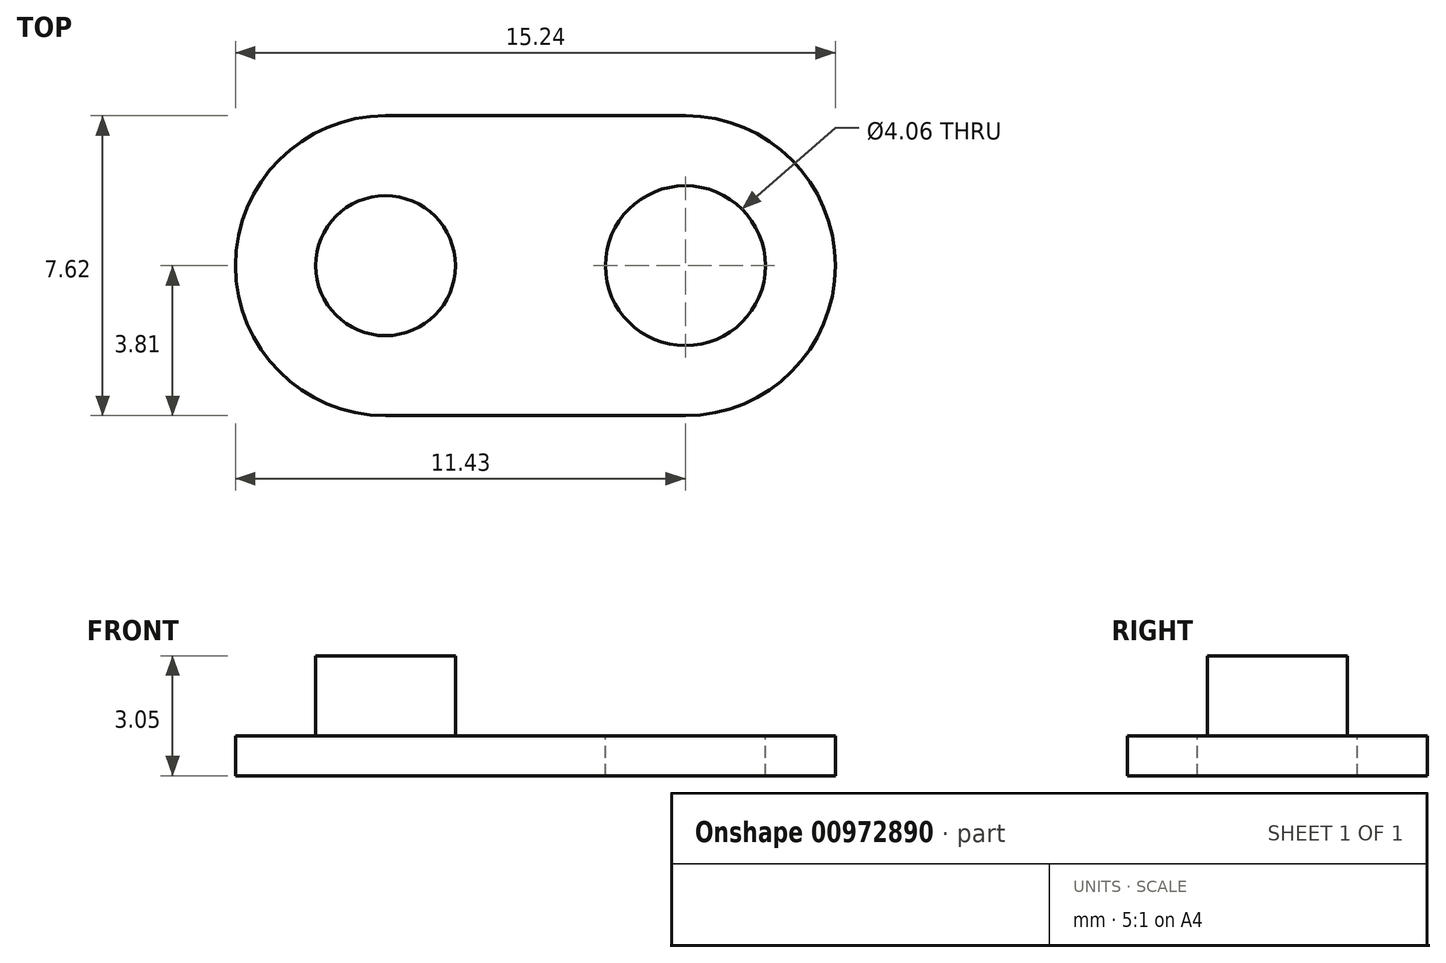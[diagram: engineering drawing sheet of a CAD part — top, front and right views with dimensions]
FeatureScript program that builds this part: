
annotation { "Feature Type Name" : "Feature", "Feature Type Description" : "" }
export const myFeature = defineFeature(function(context is Context, id is Id, definition is map)
    precondition{}
    {
        {
            var Q0;
            Q0=qCreatedBy(makeId("Top.planeOp"),FACE);
            var sketch = newSketch(context, id + "F0", { "sketchPlane" : qUnion([Q0])});
            skPoint(sketch, "E0", {"position": v(-3.81, 0) * mm});
            skPoint(sketch, "E1", {"position": v(3.81, 0) * mm});
            skCircle(sketch, "E2", {"center": v(-3.81, 0) * mm, "radius": 3.81 * mm});
            skCircle(sketch, "E3", {"center": v(3.81, 0) * mm, "radius": 3.81 * mm});
            skLineSegment(sketch, "E4", {"start": v(-3.8, -3.81) * mm, "end": v(3.81, -3.81) * mm});
            skLineSegment(sketch, "E5", {"start": v(-3.81, 3.81) * mm, "end": v(3.8, 3.81) * mm});
            skSolve(sketch);
        }
        {
            var Q0;
            {var subQ0=sQuery(id+"F0.wireOp",EDGE,"E2");var subQ1=makeQuery(id+"F0.imprint","INTERSECT",VERTEX,{"derivedFrom":[subQ0,sQuery(id+"F0.wireOp",EDGE,"E5")]});Q0=makeQuery(id+"F0.imprint","IMPRINT",FACE,{"disambiguationData":[TD([[makeQuery(id+"F0.imprint","IMPRINT",EDGE,{"disambiguationData":[TD([[subQ1,1.0]])],"derivedFrom":subQ0}),1.0]])]});}
            var Q1;
            {var subQ0=sQuery(id+"F0.wireOp",EDGE,"E3");var subQ1=makeQuery(id+"F0.imprint","INTERSECT",VERTEX,{"derivedFrom":[subQ0,sQuery(id+"F0.wireOp",EDGE,"E5")]});Q1=makeQuery(id+"F0.imprint","IMPRINT",FACE,{"disambiguationData":[TD([[makeQuery(id+"F0.imprint","IMPRINT",EDGE,{"disambiguationData":[TD([[subQ1,-1.0]])],"derivedFrom":subQ0}),1.0]])]});}
            var Q2;
            {var subQ0=sQuery(id+"F0.wireOp",EDGE,"E4");Q2=makeQuery(id+"F0.imprint","IMPRINT",FACE,{"disambiguationData":[TD([[makeQuery(id+"F0.imprint","IMPRINT",EDGE,{"derivedFrom":subQ0}),1.0]])]});}
            var Q3;
            {var subQ0=sQuery(id+"F0.wireOp",EDGE,"E5");Q3=makeQuery(id+"F0.imprint","IMPRINT",FACE,{"disambiguationData":[TD([[makeQuery(id+"F0.imprint","IMPRINT",EDGE,{"derivedFrom":subQ0}),-1.0]])]});}
            extrude(context, id + "F1", {"entities" : qUnion([Q0, Q1, Q2, Q3]), "depth" : 1.02 * mm, "offsetDistance" : 25.4 * mm});
        }
        {
            var Q0;
            Q0=makeQuery(id+"F1.opExtrude","CAP_FACE",FACE,{"disambiguationData":[OSD([sQuery(id+"F0.wireOp",EDGE,"E2"),sQuery(id+"F0.wireOp",EDGE,"E3"),sQuery(id+"F0.wireOp",EDGE,"E4"),sQuery(id+"F0.wireOp",EDGE,"E5")])],"isStart":false});
            var sketch = newSketch(context, id + "F2", { "sketchPlane" : qUnion([Q0])});
            skPoint(sketch, "E6", {"position": v(3.81, 0) * mm});
            skSolve(sketch);
        }
        {
            var Q0;
            Q0=sQuery(id+"F2.wireOp",VERTEX,"E6");
            var Q1;
            Q1=makeQuery(id+"F1.opExtrude","SWEPT_BODY",BODY,{"disambiguationData":[OSD([sQuery(id+"F0.wireOp",EDGE,"E2"),sQuery(id+"F0.wireOp",EDGE,"E3"),sQuery(id+"F0.wireOp",EDGE,"E4"),sQuery(id+"F0.wireOp",EDGE,"E5")])]});
            hole(context, id + "F3", {"style" : HoleStyle.SIMPLE, "endStyle" : HoleEndStyle.THROUGH, "holeDiameter" : 4.06 * mm, "majorDiameter" : 6.35 * mm, "isTappedThrough" : true, "tappedDepth" : 12.7 * mm, "tapClearance" : 3, "locations" : qUnion([Q0]), "scope" : qUnion([Q1])});
        }
        {
            var Q0;
            Q0=makeQuery(id+"F1.opExtrude","CAP_FACE",FACE,{"disambiguationData":[OSD([sQuery(id+"F0.wireOp",EDGE,"E2"),sQuery(id+"F0.wireOp",EDGE,"E3"),sQuery(id+"F0.wireOp",EDGE,"E4"),sQuery(id+"F0.wireOp",EDGE,"E5")])],"isStart":false});
            var sketch = newSketch(context, id + "F4", { "sketchPlane" : qUnion([Q0])});
            skPoint(sketch, "E7", {"position": v(-3.81, 0) * mm});
            skCircle(sketch, "E8", {"center": v(-3.81, 0) * mm, "radius": 1.78 * mm});
            skSolve(sketch);
        }
        {
            var Q0;
            Q0=makeQuery(id+"F4.imprint","IMPRINT",FACE,{"disambiguationData":[TD([[makeQuery(id+"F4.imprint","IMPRINT",EDGE,{"derivedFrom":sQuery(id+"F4.wireOp",EDGE,"E8")}),1.0]])]});
            extrude(context, id + "F5", {"entities" : qUnion([Q0]), "operationType" : NewBodyOperationType.ADD, "depth" : 2.03 * mm, "offsetDistance" : 25.4 * mm});
        }
    });
